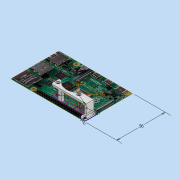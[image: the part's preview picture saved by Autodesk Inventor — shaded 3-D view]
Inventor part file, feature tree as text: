
AUTODESK INVENTOR PART (.ipt)
format: ipt  version: 2022 (Build 260153000, 153)  size: 341,504 bytes
history: native  units: mm
features: sketch x4, extrude x4, fillet x3, other x1
ambient origin geometry x8: Origin, YZ Plane, XZ Plane, XY Plane, X Axis, Y Axis, Z Axis, Center Point
bodies: Body1 (feature_tree)
feature tree (12):
  sketch  "Esquisse1"
  extrude  "Extrusion3"  Depth=56.0mm
  extrude  "Extrusion4"  Depth=3.0mm
  extrude  "Extrusion5"  Depth=6.0mm
  extrude  "Extrusion6"  Depth=30.0mm
  fillet  "Congé3"  Radius=24.0mm
  fillet  "Congé4"  Radius=4.0mm
  fillet  "Congé5"  Radius=4.0mm
  other  "Image1"
  sketch  "Esquisse3"
  sketch  "Esquisse4"
  sketch  "Esquisse5"
